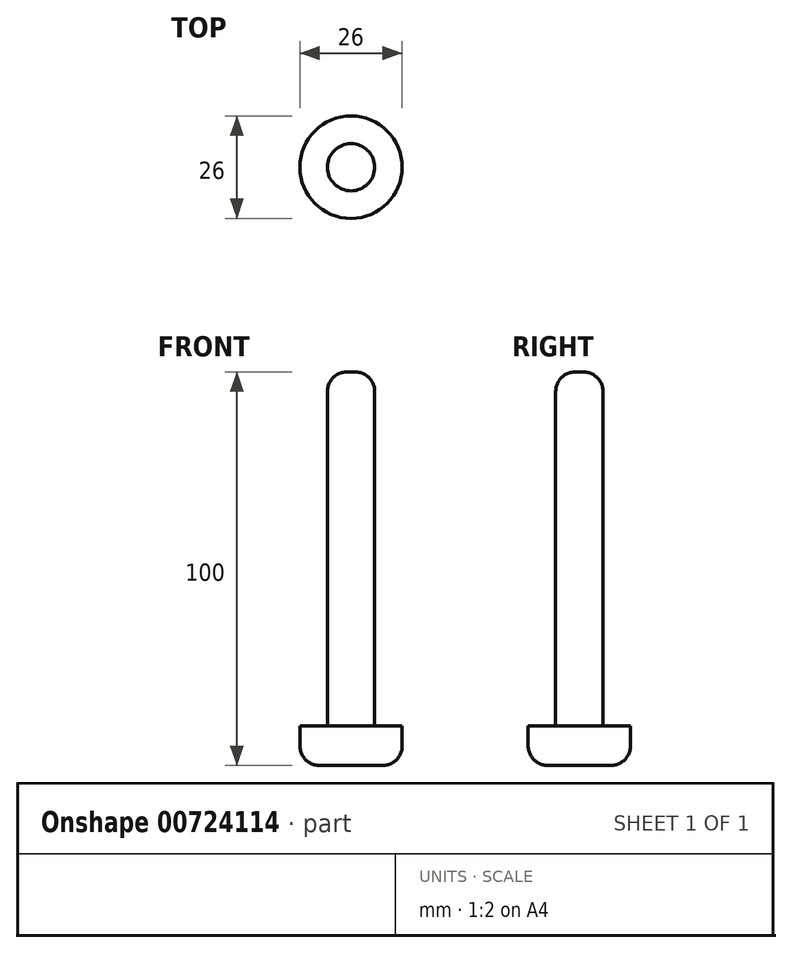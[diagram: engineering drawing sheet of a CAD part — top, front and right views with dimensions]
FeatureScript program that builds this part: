
annotation { "Feature Type Name" : "Feature", "Feature Type Description" : "" }
export const myFeature = defineFeature(function(context is Context, id is Id, definition is map)
    precondition{}
    {
        {
            var Q0;
            Q0=qCreatedBy(makeId("Top.planeOp"),FACE);
            var sketch = newSketch(context, id + "F0", { "sketchPlane" : qUnion([Q0])});
            skCircle(sketch, "E0", {"center": v(0, 0) * mm, "radius": 13 * mm});
            skSolve(sketch);
        }
        {
            var Q0;
            Q0 = qSketchRegion(id + "F0", true);
            extrude(context, id + "F1", {"entities" : qUnion([Q0]), "depth" : 10 * mm, "offsetDistance" : 25 * mm});
        }
        {
            var Q0;
            Q0=makeQuery(id+"F1.opExtrude","CAP_FACE",FACE,{"disambiguationData":[OSD([sQuery(id+"F0.wireOp",EDGE,"E0")])],"isStart":false});
            var sketch = newSketch(context, id + "F2", { "sketchPlane" : qUnion([Q0])});
            skCircle(sketch, "E1", {"center": v(0, 0) * mm, "radius": 6 * mm});
            skSolve(sketch);
        }
        {
            var Q0;
            Q0 = qSketchRegion(id + "F2", true);
            extrude(context, id + "F3", {"entities" : qUnion([Q0]), "operationType" : NewBodyOperationType.ADD, "depth" : 90 * mm, "offsetDistance" : 25 * mm});
        }
        {
            var Q0;
            Q0=makeQuery(id+"F1.opExtrude","CAP_FACE",FACE,{"disambiguationData":[OSD([sQuery(id+"F0.wireOp",EDGE,"E0")])],"isStart":true});
            fillet(context, id + "F4", {"entities" : qUnion([Q0]), "radius" : 5 * mm, "tangentPropagation" : true, "allowEdgeOverflow" : false});
        }
        {
            var Q0;
            Q0=makeQuery(id+"F3.opExtrude","CAP_EDGE",EDGE,{"disambiguationData":[OSD([sQuery(id+"F2.wireOp",EDGE,"E1")])],"isStart":false});
            fillet(context, id + "F5", {"entities" : qUnion([Q0]), "radius" : 5 * mm, "tangentPropagation" : true, "allowEdgeOverflow" : false});
        }
    });
